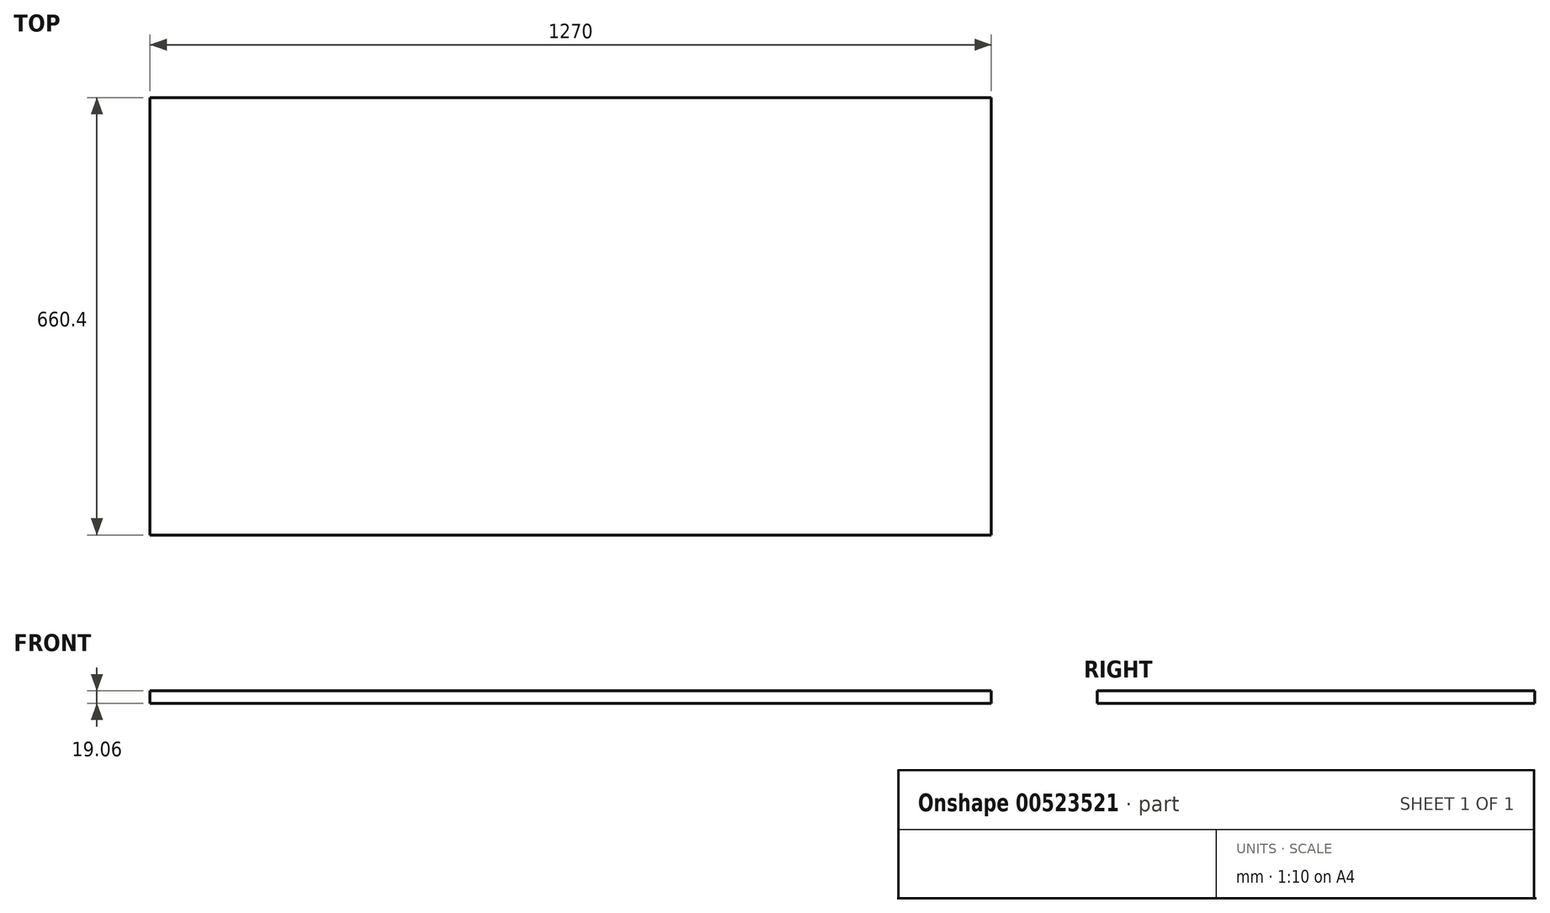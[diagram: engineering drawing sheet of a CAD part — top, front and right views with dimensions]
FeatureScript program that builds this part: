
annotation { "Feature Type Name" : "Feature", "Feature Type Description" : "" }
export const myFeature = defineFeature(function(context is Context, id is Id, definition is map)
    precondition{}
    {
        {
            var Q0;
            Q0=qCreatedBy(makeId("Top.planeOp"),FACE);
            var sketch = newSketch(context, id + "F0", { "sketchPlane" : qUnion([Q0])});
            skLineSegment(sketch, "E0.bottom", {"start": v(-635, 330.2) * mm, "end": v(635, 330.2) * mm});
            skLineSegment(sketch, "E0.top", {"start": v(-635, -330.2) * mm, "end": v(635, -330.2) * mm});
            skLineSegment(sketch, "E0.left", {"start": v(-635, 330.2) * mm, "end": v(-635, -330.2) * mm});
            skLineSegment(sketch, "E0.right", {"start": v(635, 330.2) * mm, "end": v(635, -330.2) * mm});
            skPoint(sketch, "E0.middle", {"position": v(0, 0) * mm});
            skSolve(sketch);
        }
        {
            var Q0;
            Q0=makeQuery(id+"F0.imprint","IMPRINT",FACE,{"disambiguationData":[TD([[makeQuery(id+"F0.imprint","IMPRINT",EDGE,{"derivedFrom":sQuery(id+"F0.wireOp",EDGE,"E0.bottom")}),-1.0]])]});
            extrude(context, id + "F1", {"entities" : qUnion([Q0]), "endBound" : BoundingType.SYMMETRIC, "depth" : 19.05 * mm, "offsetDistance" : 25.4 * mm});
        }
    });
